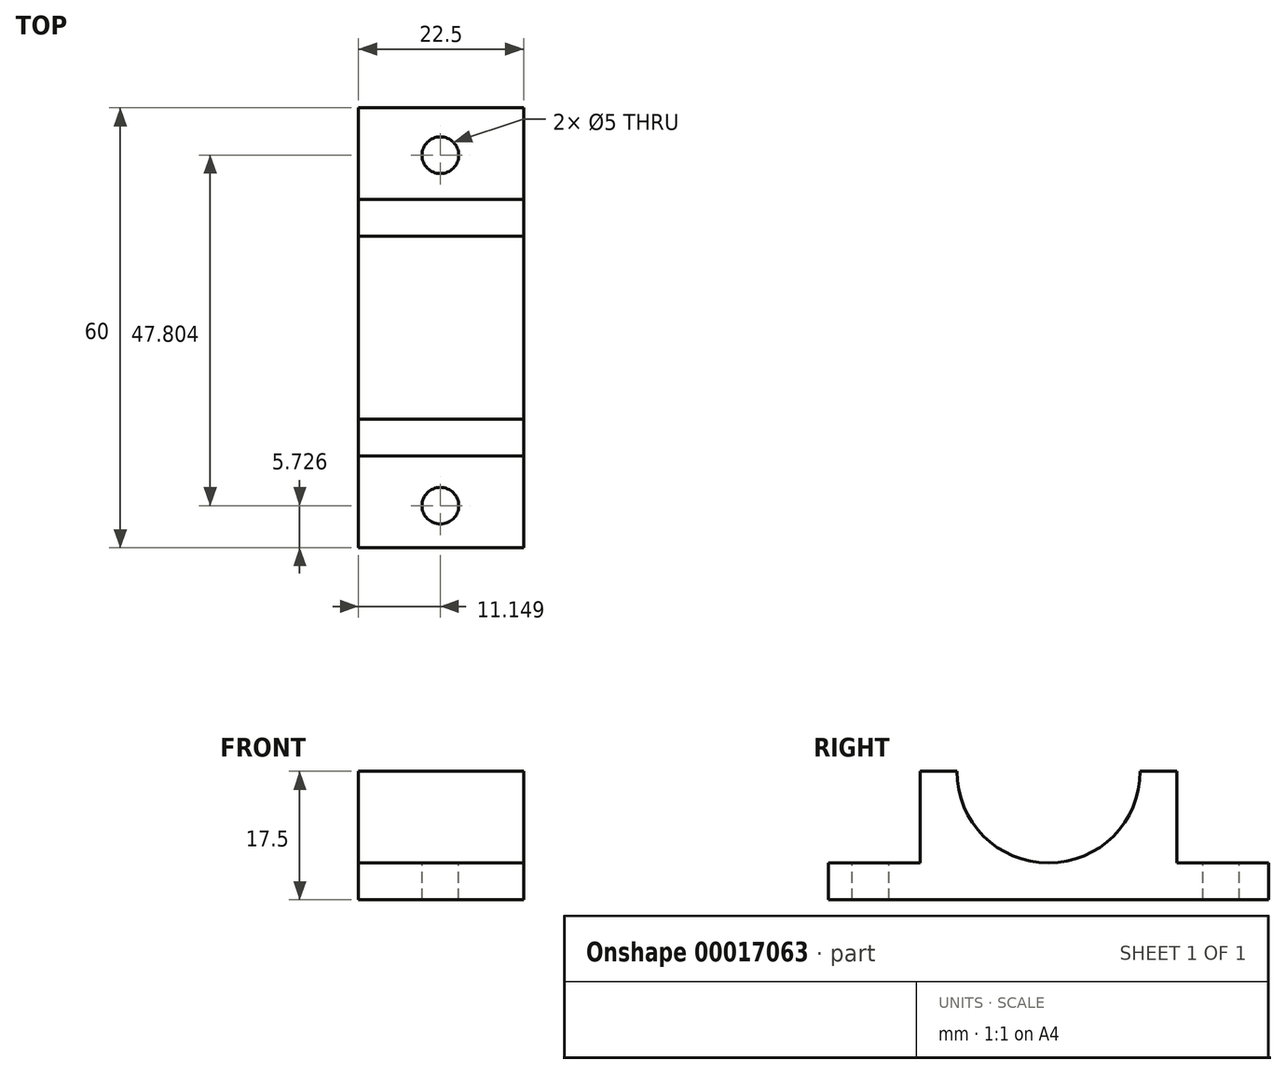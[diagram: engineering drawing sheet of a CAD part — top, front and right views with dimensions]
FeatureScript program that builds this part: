
annotation { "Feature Type Name" : "Feature", "Feature Type Description" : "" }
export const myFeature = defineFeature(function(context is Context, id is Id, definition is map)
    precondition{}
    {
        {
            var Q0;
            Q0=qCreatedBy(makeId("Right.planeOp"),FACE);
            var sketch = newSketch(context, id + "F0", { "sketchPlane" : qUnion([Q0])});
            skLineSegment(sketch, "E0", {"start": v(-78.85, -21.65) * mm, "end": v(-18.85, -21.65) * mm});
            skLineSegment(sketch, "E1", {"start": v(-18.85, -21.65) * mm, "end": v(-18.85, -16.65) * mm});
            skLineSegment(sketch, "E2", {"start": v(-18.85, -16.65) * mm, "end": v(-31.35, -16.65) * mm});
            skLineSegment(sketch, "E3", {"start": v(-78.85, -21.65) * mm, "end": v(-78.85, -16.65) * mm});
            skLineSegment(sketch, "E4", {"start": v(-78.85, -16.65) * mm, "end": v(-66.35, -16.65) * mm});
            skLineSegment(sketch, "E5", {"start": v(-66.35, -16.65) * mm, "end": v(-66.35, -4.15) * mm});
            skLineSegment(sketch, "E6", {"start": v(-66.35, -4.15) * mm, "end": v(-61.35, -4.15) * mm});
            skLineSegment(sketch, "E7", {"start": v(-31.35, -16.65) * mm, "end": v(-31.35, -4.15) * mm});
            skLineSegment(sketch, "E8", {"start": v(-31.35, -4.15) * mm, "end": v(-36.35, -4.15) * mm});
            skArc(sketch, "E9", {"start": v(-61.35, -4.15) * mm, "mid": v(-48.85, -16.65) * mm, "end": v(-36.35, -4.15) * mm});
            skSolve(sketch);
        }
        {
            var Q0;
            Q0 = qSketchRegion(id + "F0", true);
            extrude(context, id + "F1", {"entities" : qUnion([Q0]), "depth" : 22.5 * mm});
        }
        {
            var Q0;
            Q0=makeQuery(id+"F1.opExtrude","SWEPT_FACE",FACE,{"disambiguationData":[OSD([sQuery(id+"F0.wireOp",EDGE,"E2")])]});
            var sketch = newSketch(context, id + "F2", { "sketchPlane" : qUnion([Q0])});
            skCircle(sketch, "E10", {"center": v(11.15, -25.32) * mm, "radius": 2.5 * mm});
            skCircle(sketch, "E11", {"center": v(11.15, -73.12) * mm, "radius": 2.5 * mm});
            skSolve(sketch);
        }
        {
            var Q0;
            Q0 = qSketchRegion(id + "F2", true);
            extrude(context, id + "F3", {"entities" : qUnion([Q0]), "operationType" : NewBodyOperationType.REMOVE, "oppositeDirection" : true, "depth" : 5 * mm});
        }
    });
